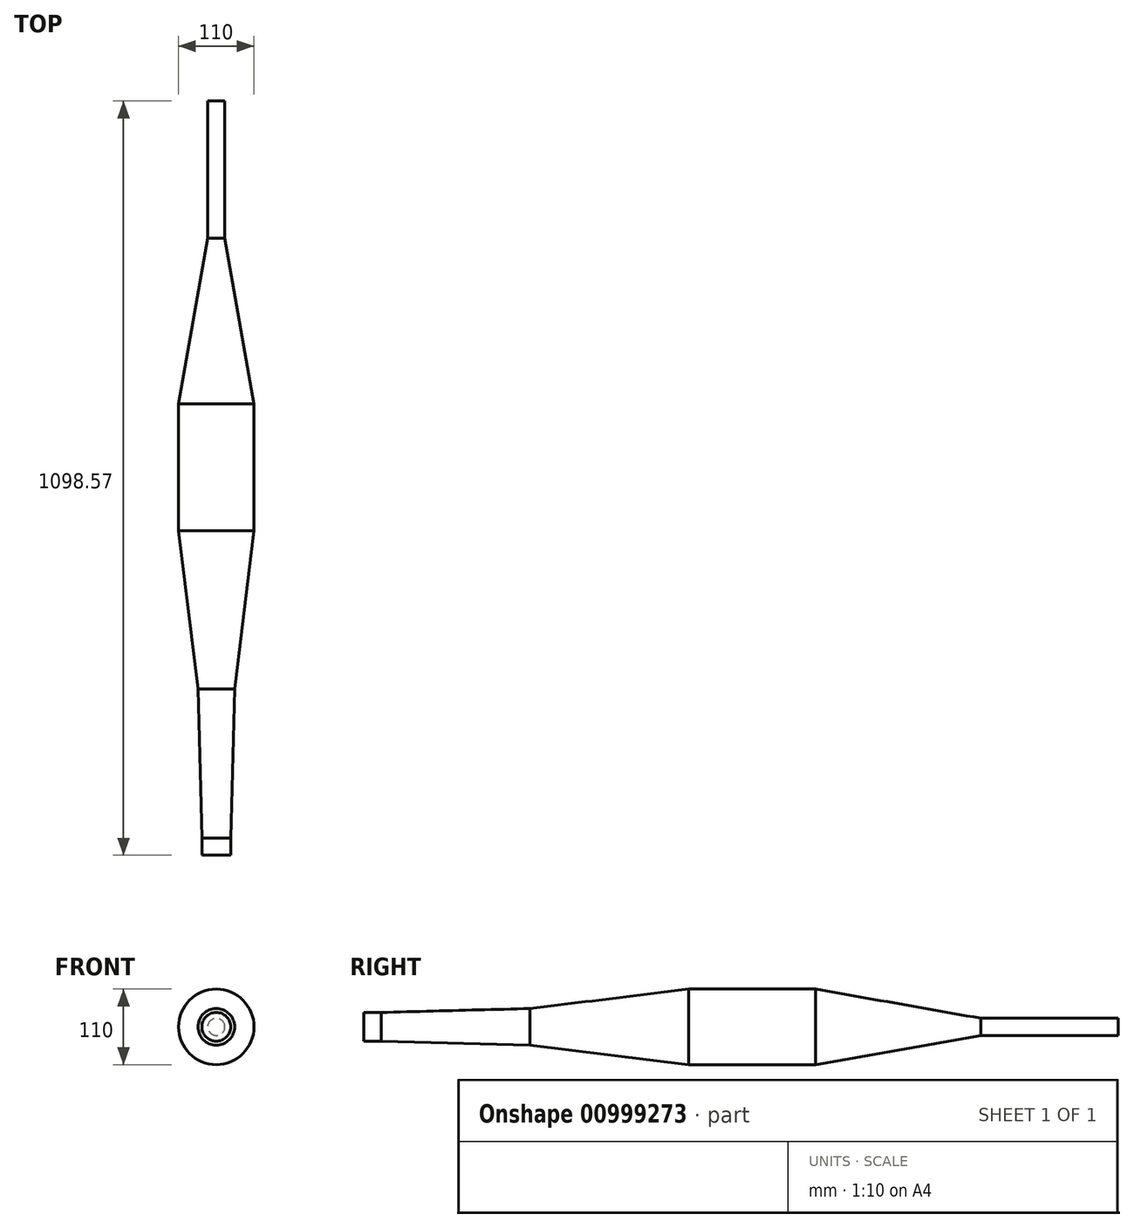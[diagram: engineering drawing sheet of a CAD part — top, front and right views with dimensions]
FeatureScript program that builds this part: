
annotation { "Feature Type Name" : "Feature", "Feature Type Description" : "" }
export const myFeature = defineFeature(function(context is Context, id is Id, definition is map)
    precondition{}
    {
        {
            var Q0;
            Q0=qCreatedBy(makeId("Right.planeOp"),FACE);
            var sketch = newSketch(context, id + "F0", { "sketchPlane" : qUnion([Q0])});
            skLineSegment(sketch, "E0", {"start": v(21.65, -12.5) * mm, "end": v(42.65, 23.87) * mm});
            skLineSegment(sketch, "E1", {"start": v(0, 191.98) * mm, "end": v(0, 233.98) * mm});
            skLineSegment(sketch, "E2", {"start": v(0, 212.98) * mm, "end": v(242, 212.98) * mm});
            skLineSegment(sketch, "E3", {"start": v(0, 212.98) * mm, "end": v(-65, 212.98) * mm});
            skLineSegment(sketch, "E4", {"start": v(242, 239.66) * mm, "end": v(242, 186.3) * mm});
            skLineSegment(sketch, "E5", {"start": v(25, 233.98) * mm, "end": v(242, 239.66) * mm});
            skLineSegment(sketch, "E6", {"start": v(25, 191.98) * mm, "end": v(242, 186.3) * mm});
            skLineSegment(sketch, "E7", {"start": v(-51.1, 50.44) * mm, "end": v(-51.1, 27.44) * mm});
            skLineSegment(sketch, "E8", {"start": v(-51.1, 38.94) * mm, "end": v(10.5, 18.19) * mm});
            skLineSegment(sketch, "E9", {"start": v(242, 212.98) * mm, "end": v(344.06, 212.98) * mm});
            skLineSegment(sketch, "E10", {"start": v(242, 239.66) * mm, "end": v(344.06, 252.2) * mm});
            skLineSegment(sketch, "E11", {"start": v(242, 186.3) * mm, "end": v(344.06, 173.76) * mm});
            skLineSegment(sketch, "E12", {"start": v(344.06, 252.2) * mm, "end": v(344.06, 173.76) * mm});
            skLineSegment(sketch, "E13", {"start": v(344.06, 212.98) * mm, "end": v(472.63, 212.98) * mm});
            skLineSegment(sketch, "E14", {"start": v(472.63, 157.98) * mm, "end": v(472.63, 267.98) * mm});
            skLineSegment(sketch, "E15", {"start": v(344.06, 252.2) * mm, "end": v(472.63, 267.98) * mm});
            skLineSegment(sketch, "E16", {"start": v(344.06, 173.76) * mm, "end": v(472.63, 157.98) * mm});
            skLineSegment(sketch, "E17", {"start": v(472.63, 212.98) * mm, "end": v(813.5, 212.98) * mm});
            skLineSegment(sketch, "E18", {"start": v(813.5, 212.98) * mm, "end": v(898.57, 212.98) * mm});
            skLineSegment(sketch, "E19", {"start": v(898.57, 200.48) * mm, "end": v(898.57, 225.48) * mm});
            skLineSegment(sketch, "E20", {"start": v(657.54, 267.98) * mm, "end": v(969.46, 212.98) * mm, "construction": true});
            skLineSegment(sketch, "E21", {"start": v(969.46, 212.98) * mm, "end": v(657.54, 157.98) * mm, "construction": true});
            skLineSegment(sketch, "E22", {"start": v(472.63, 267.98) * mm, "end": v(657.54, 267.98) * mm});
            skLineSegment(sketch, "E23", {"start": v(472.63, 157.98) * mm, "end": v(657.54, 157.98) * mm});
            skLineSegment(sketch, "E24", {"start": v(813.5, 185.48) * mm, "end": v(813.5, 240.48) * mm});
            skLineSegment(sketch, "E25", {"start": v(657.54, 267.98) * mm, "end": v(657.54, 157.98) * mm});
            skLineSegment(sketch, "E26", {"start": v(898.57, 225.48) * mm, "end": v(1098.57, 225.48) * mm});
            skLineSegment(sketch, "E27", {"start": v(898.57, 200.48) * mm, "end": v(1098.57, 200.48) * mm});
            skLineSegment(sketch, "E28", {"start": v(1098.57, 200.48) * mm, "end": v(1098.57, 225.48) * mm});
            skLineSegment(sketch, "E29", {"start": v(657.54, 267.98) * mm, "end": v(898.57, 225.48) * mm});
            skLineSegment(sketch, "E30", {"start": v(657.54, 157.98) * mm, "end": v(898.57, 200.48) * mm});
            skLineSegment(sketch, "E31", {"start": v(21.65, -12.5) * mm, "end": v(21.65, -190.3) * mm, "construction": true});
            skArc(sketch, "E32", {"start": v(32.15, 5.69) * mm, "mid": v(97.18, -130.66) * mm, "end": v(-6.8, -240.23) * mm, "construction": true});
            skLineSegment(sketch, "E33", {"start": v(-34.52, -109.8) * mm, "end": v(77.31, -182.43) * mm, "construction": true});
            skLineSegment(sketch, "E34", {"start": v(99.7, -196.96) * mm, "end": v(54.93, -167.9) * mm});
            skArc(sketch, "E35", {"start": v(99.7, -196.96) * mm, "mid": v(119.73, -74) * mm, "end": v(42.65, 23.87) * mm});
            skArc(sketch, "E36", {"start": v(54.93, -167.9) * mm, "mid": v(70.55, -83.29) * mm, "end": v(21.65, -12.5) * mm});
            skLineSegment(sketch, "E37", {"start": v(-6.8, -240.23) * mm, "end": v(-132.56, -266.96) * mm, "construction": true});
            skLineSegment(sketch, "E38", {"start": v(1.35, -278.6) * mm, "end": v(-14.95, -201.88) * mm});
            skLineSegment(sketch, "E39", {"start": v(-14.95, -201.88) * mm, "end": v(-144, -213.17) * mm});
            skLineSegment(sketch, "E40", {"start": v(1.35, -278.6) * mm, "end": v(-121.12, -320.76) * mm});
            skLineSegment(sketch, "E41", {"start": v(-144, -213.17) * mm, "end": v(-121.12, -320.76) * mm});
            skLineSegment(sketch, "E42", {"start": v(77.31, -182.43) * mm, "end": v(-6.8, -240.23) * mm, "construction": true});
            skArc(sketch, "E43", {"start": v(-14.95, -201.88) * mm, "mid": v(23.13, -191.34) * mm, "end": v(54.93, -167.9) * mm});
            skArc(sketch, "E44", {"start": v(1.35, -278.6) * mm, "mid": v(57.98, -246.75) * mm, "end": v(99.7, -196.96) * mm});
            skLineSegment(sketch, "E45", {"start": v(-132.56, -266.96) * mm, "end": v(-317.47, -266.96) * mm, "construction": true});
            skLineSegment(sketch, "E46", {"start": v(-328.9, -320.76) * mm, "end": v(-306.03, -213.17) * mm});
            skLineSegment(sketch, "E47", {"start": v(-328.9, -320.76) * mm, "end": v(-132.56, -266.96) * mm, "construction": true});
            skLineSegment(sketch, "E48", {"start": v(-317.47, -266.96) * mm, "end": v(-121.12, -320.76) * mm, "construction": true});
            skLineSegment(sketch, "E49", {"start": v(-306.03, -213.17) * mm, "end": v(-144, -213.17) * mm});
            skLineSegment(sketch, "E50", {"start": v(-121.12, -320.76) * mm, "end": v(-328.9, -320.76) * mm});
            skLineSegment(sketch, "E51", {"start": v(-622.57, -202.11) * mm, "end": v(-306.03, -213.17) * mm, "construction": true});
            skLineSegment(sketch, "E52", {"start": v(-622.57, -202.11) * mm, "end": v(-328.9, -320.76) * mm, "construction": true});
            skLineSegment(sketch, "E53", {"start": v(969.46, 212.98) * mm, "end": v(657.54, 212.98) * mm, "construction": true});
            skLineSegment(sketch, "E54", {"start": v(-317.47, -266.96) * mm, "end": v(-622.57, -202.11) * mm, "construction": true});
            skLineSegment(sketch, "E55", {"start": v(-555.83, -229.08) * mm, "end": v(-550.63, -204.62) * mm});
            skLineSegment(sketch, "E56", {"start": v(-550.63, -204.62) * mm, "end": v(-746.26, -163.04) * mm});
            skLineSegment(sketch, "E57", {"start": v(-746.26, -163.04) * mm, "end": v(-751.46, -187.5) * mm});
            skLineSegment(sketch, "E58", {"start": v(-751.46, -187.5) * mm, "end": v(-555.83, -229.08) * mm});
            skLineSegment(sketch, "E59", {"start": v(-550.63, -204.62) * mm, "end": v(-306.03, -213.17) * mm});
            skLineSegment(sketch, "E60", {"start": v(-555.83, -229.08) * mm, "end": v(-328.9, -320.76) * mm});
            skLineSegment(sketch, "E61", {"start": v(42.65, 23.87) * mm, "end": v(21, 36.37) * mm});
            skLineSegment(sketch, "E62", {"start": v(21, 36.37) * mm, "end": v(0, 0) * mm});
            skLineSegment(sketch, "E63", {"start": v(0, 0) * mm, "end": v(21.65, -12.5) * mm});
            skLineSegment(sketch, "E64", {"start": v(0, 212.98) * mm, "end": v(25, 212.98) * mm});
            skLineSegment(sketch, "E65", {"start": v(25, 233.98) * mm, "end": v(25, 191.98) * mm});
            skLineSegment(sketch, "E66", {"start": v(0, 233.98) * mm, "end": v(25, 233.98) * mm});
            skLineSegment(sketch, "E67", {"start": v(0, 191.98) * mm, "end": v(25, 191.98) * mm});
            skLineSegment(sketch, "E68", {"start": v(-51.1, 27.44) * mm, "end": v(0, 0) * mm});
            skLineSegment(sketch, "E69", {"start": v(-51.1, 50.44) * mm, "end": v(21, 36.37) * mm});
            skLineSegment(sketch, "E70", {"start": v(10.5, 18.19) * mm, "end": v(32.15, 5.69) * mm});
            skLineSegment(sketch, "E71", {"start": v(898.57, 212.98) * mm, "end": v(1098.57, 212.98) * mm});
            skLineSegment(sketch, "E72", {"start": v(657.54, 212.98) * mm, "end": v(657.54, 60.58) * mm, "construction": true});
            skLineSegment(sketch, "E73", {"start": v(657.54, 60.58) * mm, "end": v(929.7, 60.58) * mm});
            skLineSegment(sketch, "E74", {"start": v(657.54, 212.98) * mm, "end": v(929.7, 60.58) * mm, "construction": true});
            skSolve(sketch);
        }
        {
            var Q0;
            {var subQ2=sQuery(id+"F0.wireOp",EDGE,"E64");Q0=makeQuery(id+"F0.imprint","IMPRINT",FACE,{"disambiguationData":[TD([[makeQuery(id+"F0.imprint","IMPRINT",EDGE,{"derivedFrom":subQ2}),1.0]])]});}
            var Q1;
            {var subQ0=sQuery(id+"F0.wireOp",EDGE,"E2");Q1=makeQuery(id+"F0.imprint","IMPRINT",FACE,{"disambiguationData":[TD([[makeQuery(id+"F0.imprint","IMPRINT",EDGE,{"derivedFrom":subQ0}),1.0]])]});}
            var Q2;
            {var subQ0=sQuery(id+"F0.wireOp",EDGE,"E9");Q2=makeQuery(id+"F0.imprint","IMPRINT",FACE,{"disambiguationData":[TD([[makeQuery(id+"F0.imprint","IMPRINT",EDGE,{"derivedFrom":subQ0}),1.0]])]});}
            var Q3;
            {var subQ0=sQuery(id+"F0.wireOp",EDGE,"E13");Q3=makeQuery(id+"F0.imprint","IMPRINT",FACE,{"disambiguationData":[TD([[makeQuery(id+"F0.imprint","IMPRINT",EDGE,{"derivedFrom":subQ0}),1.0]])]});}
            var Q4;
            {var subQ3=sQuery(id+"F0.wireOp",EDGE,"E22");Q4=makeQuery(id+"F0.imprint","IMPRINT",FACE,{"disambiguationData":[TD([[makeQuery(id+"F0.imprint","IMPRINT",EDGE,{"derivedFrom":subQ3}),-1.0]])]});}
            var Q5;
            {var subQ1=sQuery(id+"F0.wireOp",EDGE,"E17");var subQ3=sQuery(id+"F0.wireOp",EDGE,"E25");var subQ4=makeQuery(id+"F0.imprint","INTERSECT",VERTEX,{"derivedFrom":[subQ1,subQ3]});Q5=makeQuery(id+"F0.imprint","IMPRINT",FACE,{"disambiguationData":[TD([[makeQuery(id+"F0.imprint","IMPRINT",EDGE,{"disambiguationData":[TD([[subQ4,-1.0]])],"derivedFrom":subQ1}),1.0]])]});}
            var Q6;
            {var subQ0=sQuery(id+"F0.wireOp",EDGE,"E18");Q6=makeQuery(id+"F0.imprint","IMPRINT",FACE,{"disambiguationData":[TD([[makeQuery(id+"F0.imprint","IMPRINT",EDGE,{"derivedFrom":subQ0}),1.0]])]});}
            var Q7;
            {var subQ2=sQuery(id+"F0.wireOp",EDGE,"E26");Q7=makeQuery(id+"F0.imprint","IMPRINT",FACE,{"disambiguationData":[TD([[makeQuery(id+"F0.imprint","IMPRINT",EDGE,{"derivedFrom":subQ2}),-1.0]])]});}
            var Q8;
            Q8=sQuery(id+"F0.wireOp",EDGE,"E3");
            revolve(context, id + "F1", {"surfaceOperationType" : NewSurfaceOperationType.NEW, "entities" : qUnion([Q0, Q1, Q2, Q3, Q4, Q5, Q6, Q7]), "axis" : qUnion([Q8]), "revolveType" : RevolveType.FULL});
        }
        {
            var Q0;
            {var subQ0=sQuery(id+"F0.wireOp",EDGE,"E61");Q0=makeQuery(id+"F0.imprint","IMPRINT",FACE,{"disambiguationData":[TD([[makeQuery(id+"F0.imprint","IMPRINT",EDGE,{"derivedFrom":subQ0}),1.0]])]});}
            var Q1;
            Q1=sQuery(id+"F0.wireOp",EDGE,"E61");
            var Q2;
            Q2=sQuery(id+"F0.wireOp",EDGE,"E70");
            revolve(context, id + "F2", {"bodyType" : ToolBodyType.SURFACE, "surfaceOperationType" : NewSurfaceOperationType.NEW, "entities" : qUnion([Q0]), "surfaceEntities" : qUnion([Q1]), "axis" : qUnion([Q2]), "revolveType" : RevolveType.FULL});
        }
        {
            var Q0;
            Q0=sQuery(id+"F0.wireOp",EDGE,"E34");
            var Q1;
            {var subQ0=sQuery(id+"F0.wireOp",EDGE,"E36");Q1=makeQuery(id+"F0.imprint","IMPRINT",FACE,{"disambiguationData":[TD([[makeQuery(id+"F0.imprint","IMPRINT",EDGE,{"derivedFrom":subQ0}),-1.0]])]});}
            cPlane(context, id + "F3", {"entities" : qUnion([Q0, Q1]), "cplaneType" : CPlaneType.LINE_ANGLE, "offset" : 0 * mm, "angle" : 90 * degree, "width" : 152.4 * mm, "height" : 152.4 * mm});
        }
        {
            var Q0;
            Q0=qCreatedBy(id+"F3.planeOp",FACE);
            var sketch = newSketch(context, id + "F4", { "sketchPlane" : qUnion([Q0])});
            skCircle(sketch, "E75", {"center": v(0, -164.2) * mm, "radius": 26.68 * mm});
            skSolve(sketch);
        }
        {
            var Q0;
            Q0=makeQuery(id+"F4.imprint","IMPRINT",FACE,{"disambiguationData":[TD([[makeQuery(id+"F4.imprint","IMPRINT",EDGE,{"derivedFrom":sQuery(id+"F4.wireOp",EDGE,"E75")}),1.0]])]});
            var Q1;
            Q1=makeQuery(id+"F2.opRevolve","SWEPT_BODY",BODY,{"disambiguationData":[OSD([sQuery(id+"F0.wireOp",EDGE,"E61")])]});
            var Q2;
            Q2=makeQuery(id+"F2.opRevolve","SWEPT_EDGE",EDGE,{"disambiguationData":[OSD([sQuery(id+"F0.wireOp",VERTEX,"E61.start")])]});
            var Q3;
            Q3=sQuery(id+"F4.wireOp",EDGE,"E75");
            var Q4;
            Q4=sQuery(id+"F0.wireOp",EDGE,"E35");
            var Q5;
            Q5=sQuery(id+"F0.wireOp",EDGE,"E36");
            loft(context, id + "F5", {"bodyType" : ToolBodyType.SURFACE, "operationType" : NewBodyOperationType.ADD, "surfaceOperationType" : NewSurfaceOperationType.ADD, "addGuides" : true, "sheetProfilesArray" : [{ "sheetProfileEntities" : qUnion([Q0]) }, { "sheetProfileEntities" : qUnion([Q1]) }], "wireProfilesArray" : [{ "wireProfileEntities" : qUnion([Q2]) }, { "wireProfileEntities" : qUnion([Q3]) }], "guidesArray" : [{ "guideEntities" : qUnion([Q4]), "guideDerivativeType" : LoftGuideDerivativeType.DEFAULT, "guideDerivativeMagnitude" : 1 }, { "guideEntities" : qUnion([Q5]), "guideDerivativeType" : LoftGuideDerivativeType.DEFAULT, "guideDerivativeMagnitude" : 1 }]});
        }
        {
            var Q0;
            Q0=sQuery(id+"F0.wireOp",EDGE,"E38");
            var Q1;
            {var subQ5=sQuery(id+"F0.wireOp",EDGE,"E43");Q1=makeQuery(id+"F0.imprint","IMPRINT",FACE,{"disambiguationData":[TD([[makeQuery(id+"F0.imprint","IMPRINT",EDGE,{"derivedFrom":subQ5}),-1.0]])]});}
            cPlane(context, id + "F6", {"entities" : qUnion([Q0, Q1]), "cplaneType" : CPlaneType.LINE_ANGLE, "offset" : 25.4 * mm, "angle" : 90 * degree, "width" : 152.4 * mm, "height" : 152.4 * mm});
        }
        {
            var Q0;
            Q0=qCreatedBy(id+"F6.planeOp",FACE);
            var sketch = newSketch(context, id + "F7", { "sketchPlane" : qUnion([Q0])});
            skCircle(sketch, "E76", {"center": v(0, -233.57) * mm, "radius": 39.21 * mm});
            skSolve(sketch);
        }
        {
            var Q1;
            Q1=makeQuery(id+"F5.opLoft","CAP_FACE",FACE,{"disambiguationData":[OSD([makeQuery(id+"F4.imprint","IMPRINT",FACE,{"disambiguationData":[TD([[makeQuery(id+"F4.imprint","IMPRINT",EDGE,{"derivedFrom":sQuery(id+"F4.wireOp",EDGE,"E75")}),1.0]])]})])],"isStart":true});
            var Q2;
            Q2=makeQuery(id+"F7.imprint","IMPRINT",FACE,{"disambiguationData":[TD([[makeQuery(id+"F7.imprint","IMPRINT",EDGE,{"derivedFrom":sQuery(id+"F7.wireOp",EDGE,"E76")}),1.0]])]});
            var Q3;
            Q3=sQuery(id+"F7.wireOp",EDGE,"E76");
            var Q4;
            Q4=makeQuery(id+"F4.imprint","IMPRINT",FACE,{"disambiguationData":[TD([[makeQuery(id+"F4.imprint","IMPRINT",EDGE,{"derivedFrom":sQuery(id+"F4.wireOp",EDGE,"E75")}),1.0]])]});
            var Q5;
            Q5=sQuery(id+"F0.wireOp",EDGE,"E44");
            var Q6;
            Q6=sQuery(id+"F0.wireOp",EDGE,"E43");
            loft(context, id + "F8", {"bodyType" : ToolBodyType.SURFACE, "operationType" : NewBodyOperationType.ADD, "addGuides" : true, "sheetProfilesArray" : [{ "sheetProfileEntities" : qUnion([Q1]) }, { "sheetProfileEntities" : qUnion([Q2]) }], "wireProfilesArray" : [{ "wireProfileEntities" : qUnion([Q3]) }, { "wireProfileEntities" : qUnion([Q4]) }], "guidesArray" : [{ "guideEntities" : qUnion([Q5]), "guideDerivativeType" : LoftGuideDerivativeType.DEFAULT, "guideDerivativeMagnitude" : 1 }, { "guideEntities" : qUnion([Q6]), "guideDerivativeType" : LoftGuideDerivativeType.DEFAULT, "guideDerivativeMagnitude" : 1 }]});
        }
        {
            var Q0;
            Q0=sQuery(id+"F0.wireOp",EDGE,"E41");
            var Q1;
            {var subQ0=sQuery(id+"F0.wireOp",EDGE,"E37");Q1=makeQuery(id+"F0.imprint","IMPRINT",FACE,{"disambiguationData":[TD([[makeQuery(id+"F0.imprint","IMPRINT",EDGE,{"derivedFrom":subQ0}),-1.0]])]});}
            cPlane(context, id + "F9", {"entities" : qUnion([Q0, Q1]), "cplaneType" : CPlaneType.LINE_ANGLE, "offset" : 25.4 * mm, "angle" : 90 * degree, "oppositeDirection" : true, "width" : 152.4 * mm, "height" : 152.4 * mm});
        }
        {
            var Q0;
            Q0=qCreatedBy(id+"F9.planeOp",FACE);
            var sketch = newSketch(context, id + "F10", { "sketchPlane" : qUnion([Q0])});
            skCircle(sketch, "E77", {"center": v(0, -235.32) * mm, "radius": 55 * mm});
            skLineSegment(sketch, "E78", {"start": v(0, -180.32) * mm, "end": v(0, -290.32) * mm, "construction": true});
            skSolve(sketch);
        }
        {
            var Q1;
            Q1=makeQuery(id+"F8.opLoft","CAP_FACE",FACE,{"disambiguationData":[OSD([makeQuery(id+"F7.imprint","IMPRINT",FACE,{"disambiguationData":[TD([[makeQuery(id+"F7.imprint","IMPRINT",EDGE,{"derivedFrom":sQuery(id+"F7.wireOp",EDGE,"E76")}),1.0]])]})])],"isStart":true});
            var Q2;
            Q2=makeQuery(id+"F10.imprint","IMPRINT",FACE,{"disambiguationData":[TD([[makeQuery(id+"F10.imprint","IMPRINT",EDGE,{"derivedFrom":sQuery(id+"F10.wireOp",EDGE,"E77")}),1.0]])]});
            var Q3;
            Q3=sQuery(id+"F7.wireOp",EDGE,"E76");
            var Q4;
            Q4=sQuery(id+"F10.wireOp",EDGE,"E77");
            loft(context, id + "F11", {"bodyType" : ToolBodyType.SURFACE, "surfaceOperationType" : NewSurfaceOperationType.ADD, "sheetProfilesArray" : [{ "sheetProfileEntities" : qUnion([Q1]) }, { "sheetProfileEntities" : qUnion([Q2]) }], "wireProfilesArray" : [{ "wireProfileEntities" : qUnion([Q3]) }, { "wireProfileEntities" : qUnion([Q4]) }]});
        }
        {
            var Q0;
            Q0=sQuery(id+"F0.wireOp",EDGE,"E46");
            var Q1;
            {var subQ0=sQuery(id+"F0.wireOp",EDGE,"E45");Q1=makeQuery(id+"F0.imprint","IMPRINT",FACE,{"disambiguationData":[TD([[makeQuery(id+"F0.imprint","IMPRINT",EDGE,{"derivedFrom":subQ0}),-1.0]])]});}
            cPlane(context, id + "F12", {"entities" : qUnion([Q0, Q1]), "cplaneType" : CPlaneType.LINE_ANGLE, "offset" : 25.4 * mm, "angle" : 97 * degree, "width" : 152.4 * mm, "height" : 152.4 * mm});
        }
        {
            var Q0;
            Q0=qCreatedBy(id+"F12.planeOp",FACE);
            var sketch = newSketch(context, id + "F13", { "sketchPlane" : qUnion([Q0])});
            skCircle(sketch, "E79", {"center": v(31.08, -327.14) * mm, "radius": 55 * mm, "construction": true});
            skLineSegment(sketch, "E80", {"start": v(31.08, -327.14) * mm, "end": v(18.38, -327.14) * mm, "construction": true});
            skCircle(sketch, "E81", {"center": v(18.38, -327.14) * mm, "radius": 55 * mm});
            skLineSegment(sketch, "E82", {"start": v(18.38, -272.14) * mm, "end": v(18.38, -382.14) * mm, "construction": true});
            skSolve(sketch);
        }
        {
            var Q0;
            Q0=sQuery(id+"F13.wireOp",VERTEX,"E82.start");
            var Q1;
            Q1=sQuery(id+"F13.wireOp",VERTEX,"E82.end");
            var Q2;
            Q2=sQuery(id+"F10.wireOp",VERTEX,"E78.start");
            cPlane(context, id + "F14", {"entities" : qUnion([Q0, Q1, Q2]), "cplaneType" : CPlaneType.THREE_POINT, "offset" : 25.4 * mm, "width" : 152.4 * mm, "height" : 152.4 * mm});
        }
        {
            var Q0;
            Q0=qCreatedBy(id+"F14.planeOp",FACE);
            var sketch = newSketch(context, id + "F15", { "sketchPlane" : qUnion([Q0])});
            skLineSegment(sketch, "E83", {"start": v(304.85, -213.25) * mm, "end": v(143.47, -214.84) * mm});
            skSolve(sketch);
        }
        {
            var Q0;
            Q0=makeQuery(id+"F11.opLoft","CAP_FACE",FACE,{"disambiguationData":[OSD([makeQuery(id+"F10.imprint","IMPRINT",FACE,{"disambiguationData":[TD([[makeQuery(id+"F10.imprint","IMPRINT",EDGE,{"derivedFrom":sQuery(id+"F10.wireOp",EDGE,"E77")}),1.0]])]})])],"isStart":true});
            var Q1;
            Q1=makeQuery(id+"F13.imprint","IMPRINT",FACE,{"disambiguationData":[TD([[makeQuery(id+"F13.imprint","IMPRINT",EDGE,{"derivedFrom":sQuery(id+"F13.wireOp",EDGE,"E79")}),1.0]])]});
            var Q2;
            Q2=sQuery(id+"F10.wireOp",EDGE,"E77");
            var Q3;
            Q3=sQuery(id+"F13.wireOp",EDGE,"E81");
            var Q4;
            Q4=sQuery(id+"F15.wireOp",EDGE,"E83");
            loft(context, id + "F16", {"bodyType" : ToolBodyType.SURFACE, "surfaceOperationType" : NewSurfaceOperationType.ADD, "addGuides" : true, "sheetProfilesArray" : [{ "sheetProfileEntities" : qUnion([Q0]) }, { "sheetProfileEntities" : qUnion([Q1]) }], "wireProfilesArray" : [{ "wireProfileEntities" : qUnion([Q2]) }, { "wireProfileEntities" : qUnion([Q3]) }], "guidesArray" : [{ "guideEntities" : qUnion([Q4]), "guideDerivativeType" : LoftGuideDerivativeType.DEFAULT, "guideDerivativeMagnitude" : 1 }]});
        }
        {
            var Q0;
            Q0=sQuery(id+"F0.wireOp",EDGE,"E55");
            cPlane(context, id + "F17", {"entities" : qUnion([Q0]), "cplaneType" : CPlaneType.LINE_ANGLE, "offset" : 25.4 * mm, "angle" : 90 * degree, "oppositeDirection" : true, "width" : 152.4 * mm, "height" : 152.4 * mm});
        }
        {
            var Q0;
            Q0=qCreatedBy(id+"F17.planeOp",FACE);
            var sketch = newSketch(context, id + "F18", { "sketchPlane" : qUnion([Q0])});
            skCircle(sketch, "E84", {"center": v(0, -327.14) * mm, "radius": 12.5 * mm, "construction": true});
            skLineSegment(sketch, "E85", {"start": v(0, -327.14) * mm, "end": v(88.9, -327.14) * mm, "construction": true});
            skCircle(sketch, "E86", {"center": v(88.9, -327.14) * mm, "radius": 12.5 * mm});
            skSolve(sketch);
        }
        {
            var Q1;
            Q1=makeQuery(id+"F16.opLoft","CAP_FACE",FACE,{"disambiguationData":[OSD([makeQuery(id+"F13.imprint","IMPRINT",FACE,{"disambiguationData":[TD([[makeQuery(id+"F13.imprint","IMPRINT",EDGE,{"derivedFrom":sQuery(id+"F13.wireOp",EDGE,"E79")}),1.0]])]})])],"isStart":true});
            var Q2;
            Q2=makeQuery(id+"F18.imprint","IMPRINT",FACE,{"disambiguationData":[TD([[makeQuery(id+"F18.imprint","IMPRINT",EDGE,{"derivedFrom":sQuery(id+"F18.wireOp",EDGE,"E84")}),1.0]])]});
            var Q3;
            Q3=sQuery(id+"F18.wireOp",EDGE,"E86");
            var Q4;
            Q4=sQuery(id+"F13.wireOp",EDGE,"E81");
            loft(context, id + "F19", {"bodyType" : ToolBodyType.SURFACE, "surfaceOperationType" : NewSurfaceOperationType.ADD, "sheetProfilesArray" : [{ "sheetProfileEntities" : qUnion([Q1]) }, { "sheetProfileEntities" : qUnion([Q2]) }], "wireProfilesArray" : [{ "wireProfileEntities" : qUnion([Q3]) }, { "wireProfileEntities" : qUnion([Q4]) }]});
        }
        {
            var Q0;
            Q0=makeQuery(id+"F19.opLoft","CAP_FACE",FACE,{"disambiguationData":[OSD([makeQuery(id+"F18.imprint","IMPRINT",FACE,{"disambiguationData":[TD([[makeQuery(id+"F18.imprint","IMPRINT",EDGE,{"derivedFrom":sQuery(id+"F18.wireOp",EDGE,"E84")}),1.0]])]})])],"isStart":true});
            var Q1;
            Q1=sQuery(id+"F18.wireOp",EDGE,"E86");
            extrude(context, id + "F20", {"entities" : qUnion([Q0]), "bodyType" : ToolBodyType.SURFACE, "surfaceOperationType" : NewSurfaceOperationType.ADD, "surfaceEntities" : qUnion([Q1]), "depth" : 200 * mm, "offsetDistance" : 25.4 * mm});
        }
    });
